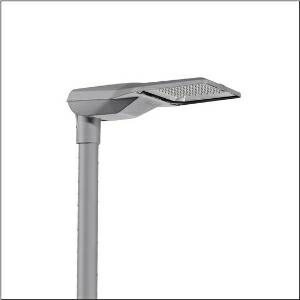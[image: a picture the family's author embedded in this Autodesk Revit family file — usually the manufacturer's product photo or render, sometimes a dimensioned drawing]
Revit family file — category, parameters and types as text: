
# Revit family: streetlight_sl_21_iq_midi___st1_0a_5xe3d61d08nb_4d1e
name_source: partatom
category: Lighting Fixtures
units: mm (PartAtom-declared; Revit-internal decimal feet)

## family parameters
Cut with Voids When Loaded = No
Host = Face
Light Source = No
Part Type = Normal
Room Calculation Point = No
Round Connector Dimension = Use Diameter
Shared = No

## types (1)
- --- (1 x LED, 20820 lm, 155.5 W, 2700K)
    Apparent Load = 155 VA
    CIE Flux Codes = 40 73 97 100 100
    Color Rendering = 70
    Color Temperature = 2700K
    Default Elevation = 1800 mm
    Description = Streetlight SL 21 iQ midi, mast luminaire, primary light control with lens, of PMMA, primary optical cover: cover, of toughened safety glass, transparent, light distribution: ST1.0a, light emission: direct distribution, primary light characteristic: asymmetric, installation type: post-top, side-entry, LED, High Power LED, rated luminous flux: 20.820lm, luminous efficacy: 134lm/W, light colour: 727, colour temperature: 2700K, control gear: iQ-Comfort, control: Auto-Match, Temp-Guard, Lumen-Switch, Night-Set, Smart-Wire, Light-Fading, Desk-Remote (wireless, voltage-free reading and setting of iQ features in the workshop via application-optimized NFC function/RFID function), optimised constant luminous flux control (CLO 2.0), pre-setting: linear dimming characteristic, mains connection: 230..240V, AC, 50/60Hz, start of lifetime: 156W, end of service life: 162W, reduction: 69W, luminaire housing, of diecast aluminium, powder-coated, Siteco® metallic grey (DB 702S), corrosivity category C5 mid according to DIN EN ISO 12944, please order mast flange separately, inclination adjustable: 0°, 5°, 10°, 15°, sealing non-destructively replaceable, multi-level sealing system, length: 644mm, width: 335mm, height: 110mm, mast flange for spigot size: 42mm (side-entry): 5XC10008XM4, 60/48mm (side-entry/post-top): 5XC10108XM2, 76/60mm (side-entry/post-top): 5XC10108XM1, mounting height: 4..8m, protection rating (complete): IP66, insulation class (complete): insulation class II (safety insulation), certification: CE, ENEC, ENEC+, VDE, impact resistance: IK10, permissible operating ambient temperature for outdoor applications: -40..+50°C, standard-compliant lighting for roads and squares, packaging unit: 1 piece

Light Distribution: ST1.0a
    Height = 111 mm
    Lamp = 1 x LED
    Lamp Light Flux = 20820 lm
    Lamp Power = 155.5 W
    Lamp count = 1
    Length = 644 mm
    Luminous efficacy = 134 lm/W
    Manufacturer = Siteco
    ModVariant = No
    Model = 5XE3D61D08NB
    Number of Poles = 1
    OnlyDefault = Yes
    Power Factor = 1
    Product Name = Streetlight SL 21 iQ midi | ST1.0a
    Product group = mast luminaire | pylon top
    ProductGroupID = 6100
    Protection Class = Protection class II
    Protection Degree = IP 66
    RLX_Detail_Level = 1
    RLX_Emergency_Light_Flux = 0 lm
    RLX_Emergency_Type = 0
    RLX_Emergency_Type_DB = No
    RlxData = <blob elided: 27197 chars, md5=995ea799>
    Socket = socket
    Standby Power = 0 W
    System Light Flux = 20820 lm
    System Power = 155 W
    Type Comments = factory setting: luminous flux: 100 % | dim-lin: 254 | 823 mA
    Type Image = l_1004298.jpg
    URL = http://relux.com
    VarID = @adj_170730
    Voltage = 0 V
    Weight = 0.00 kg
    Width = 336 mm

## geometry (parser evidence)
native form markers: Blend x4, Sweep x11
no freeform markers — native parametric forms only
